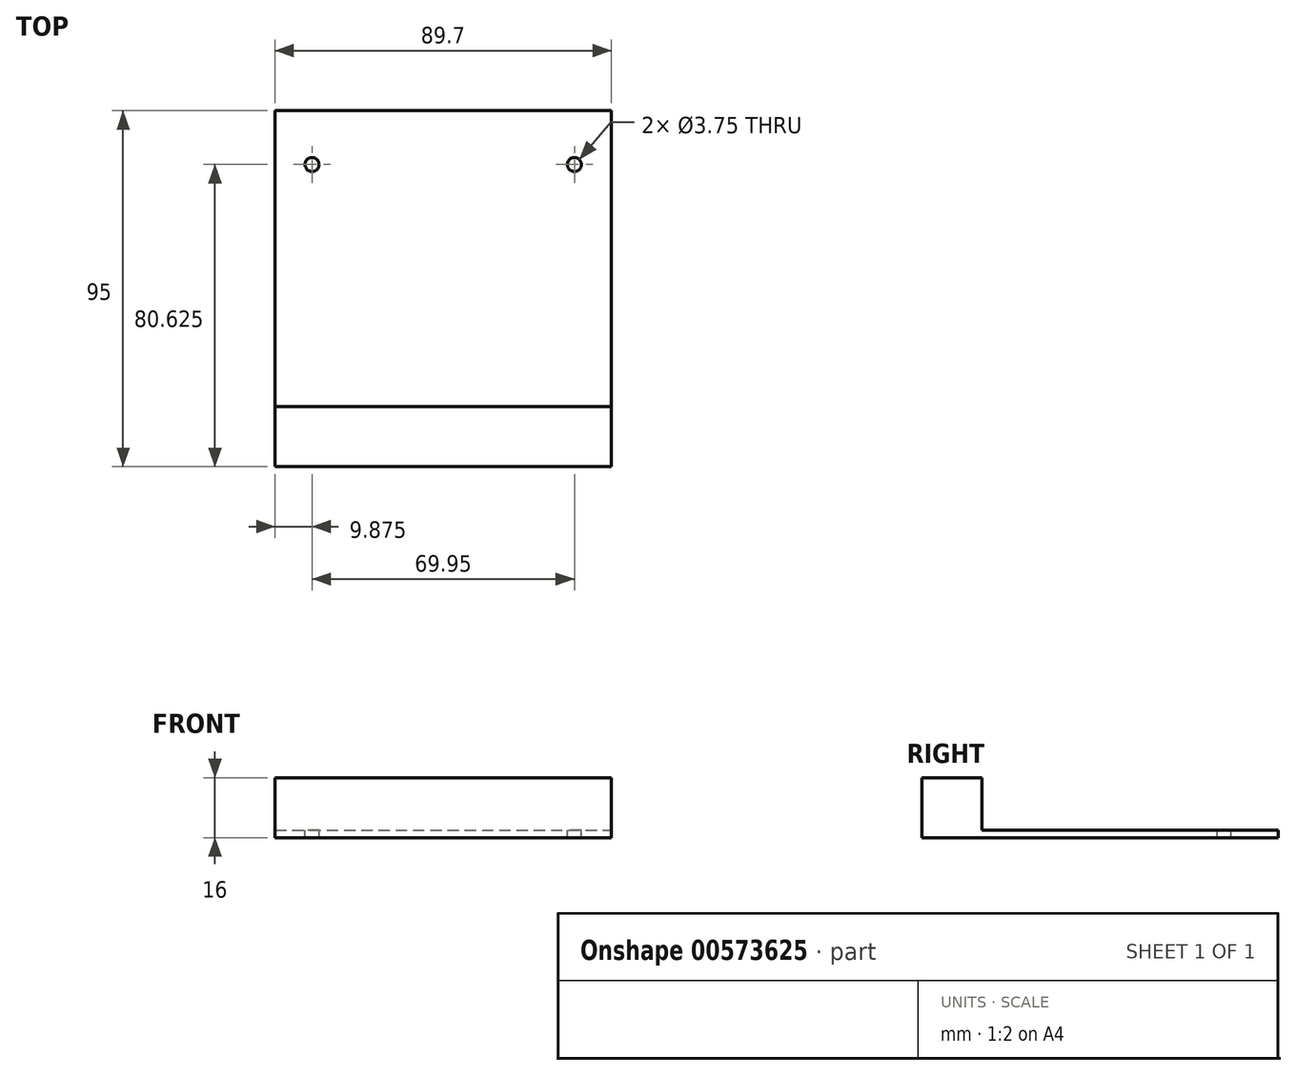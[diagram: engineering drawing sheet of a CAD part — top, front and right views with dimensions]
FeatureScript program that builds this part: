
annotation { "Feature Type Name" : "Feature", "Feature Type Description" : "" }
export const myFeature = defineFeature(function(context is Context, id is Id, definition is map)
    precondition{}
    {
        {
            var Q0;
            Q0=qCreatedBy(makeId("Top.planeOp"),FACE);
            var sketch = newSketch(context, id + "F0", { "sketchPlane" : qUnion([Q0])});
            skLineSegment(sketch, "E0.bottom", {"start": v(44.85, -47.5) * mm, "end": v(-44.85, -47.5) * mm});
            skLineSegment(sketch, "E0.top", {"start": v(44.85, 47.5) * mm, "end": v(-44.85, 47.5) * mm});
            skLineSegment(sketch, "E0.left", {"start": v(44.85, -47.5) * mm, "end": v(44.85, 47.5) * mm});
            skLineSegment(sketch, "E0.right", {"start": v(-44.85, -47.5) * mm, "end": v(-44.85, 47.5) * mm});
            skPoint(sketch, "E0.middle", {"position": v(0, 0) * mm});
            skSolve(sketch);
        }
        {
            var Q0;
            Q0 = qSketchRegion(id + "F0", true);
            extrude(context, id + "F1", {"entities" : qUnion([Q0]), "depth" : 2 * mm, "offsetDistance" : 25 * mm});
        }
        {
            var Q0;
            Q0=makeQuery(id+"F1.opExtrude","CAP_FACE",FACE,{"disambiguationData":[OSD([sQuery(id+"F0.wireOp",EDGE,"E0.bottom"),sQuery(id+"F0.wireOp",EDGE,"E0.top"),sQuery(id+"F0.wireOp",EDGE,"E0.left"),sQuery(id+"F0.wireOp",EDGE,"E0.right")])],"isStart":false});
            var sketch = newSketch(context, id + "F2", { "sketchPlane" : qUnion([Q0])});
            skLineSegment(sketch, "E1", {"start": v(0, 47.5) * mm, "end": v(0, -47.5) * mm, "construction": true});
            skCircle(sketch, "E2", {"center": v(-34.98, 33.12) * mm, "radius": 1.88 * mm});
            skCircle(sketch, "E3.MirrorC", {"center": v(34.98, 33.12) * mm, "radius": 1.88 * mm});
            skSolve(sketch);
        }
        {
            var Q0;
            Q0 = qSketchRegion(id + "F2", true);
            extrude(context, id + "F3", {"entities" : qUnion([Q0]), "operationType" : NewBodyOperationType.REMOVE, "endBound" : BoundingType.THROUGH_ALL, "oppositeDirection" : true, "depth" : 25 * mm, "offsetDistance" : 25 * mm});
        }
        {
            var Q0;
            Q0=makeQuery(id+"F1.opExtrude","CAP_FACE",FACE,{"disambiguationData":[OSD([sQuery(id+"F0.wireOp",EDGE,"E0.bottom"),sQuery(id+"F0.wireOp",EDGE,"E0.top"),sQuery(id+"F0.wireOp",EDGE,"E0.left"),sQuery(id+"F0.wireOp",EDGE,"E0.right")])],"isStart":false});
            var sketch = newSketch(context, id + "F4", { "sketchPlane" : qUnion([Q0])});
            skLineSegment(sketch, "E4.bottom", {"start": v(-44.85, -47.5) * mm, "end": v(44.85, -47.5) * mm});
            skLineSegment(sketch, "E4.top", {"start": v(-44.85, -31.5) * mm, "end": v(44.85, -31.5) * mm});
            skLineSegment(sketch, "E4.left", {"start": v(-44.85, -47.5) * mm, "end": v(-44.85, -31.5) * mm});
            skLineSegment(sketch, "E4.right", {"start": v(44.85, -47.5) * mm, "end": v(44.85, -31.5) * mm});
            skSolve(sketch);
        }
        {
            var Q0;
            Q0 = qSketchRegion(id + "F4", true);
            extrude(context, id + "F5", {"entities" : qUnion([Q0]), "operationType" : NewBodyOperationType.ADD, "depth" : 14 * mm, "offsetDistance" : 25 * mm});
        }
    });
